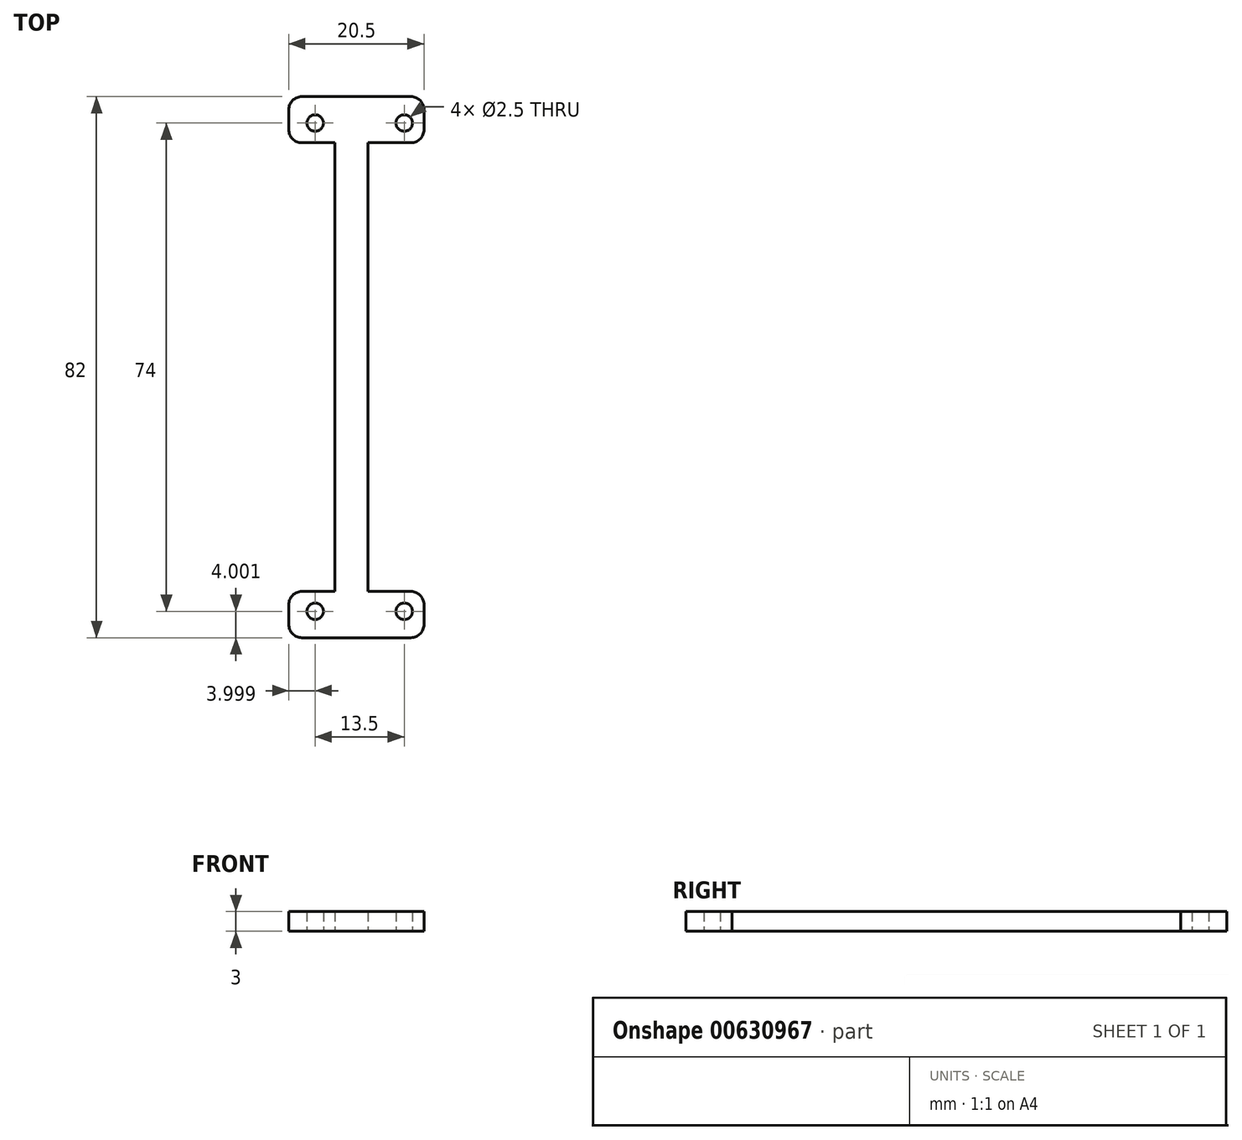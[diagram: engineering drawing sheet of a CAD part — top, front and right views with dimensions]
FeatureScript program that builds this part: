
annotation { "Feature Type Name" : "Feature", "Feature Type Description" : "" }
export const myFeature = defineFeature(function(context is Context, id is Id, definition is map)
    precondition{}
    {
        {
            var Q0;
            Q0=qCreatedBy(makeId("Top.planeOp"),FACE);
            var sketch = newSketch(context, id + "F0", { "sketchPlane" : qUnion([Q0])});
            skCircle(sketch, "E0", {"center": v(-18.35, 41.36) * mm, "radius": 1.25 * mm});
            skCircle(sketch, "E1", {"center": v(-4.85, 41.36) * mm, "radius": 1.25 * mm});
            skCircle(sketch, "E2", {"center": v(-18.35, -32.64) * mm, "radius": 1.25 * mm});
            skCircle(sketch, "E3", {"center": v(-4.85, -32.64) * mm, "radius": 1.25 * mm});
            skLineSegment(sketch, "E4", {"start": v(-20.35, 45.36) * mm, "end": v(-3.85, 45.36) * mm});
            skLineSegment(sketch, "E5", {"start": v(-1.85, 43.36) * mm, "end": v(-1.85, 40.36) * mm});
            skLineSegment(sketch, "E6", {"start": v(-3.85, 38.36) * mm, "end": v(-10.35, 38.36) * mm});
            skLineSegment(sketch, "E7", {"start": v(-10.35, 38.36) * mm, "end": v(-10.35, -29.64) * mm});
            skLineSegment(sketch, "E8", {"start": v(-10.35, -29.64) * mm, "end": v(-3.85, -29.64) * mm});
            skLineSegment(sketch, "E9", {"start": v(-1.85, -31.64) * mm, "end": v(-1.85, -34.64) * mm});
            skLineSegment(sketch, "E10", {"start": v(-3.85, -36.64) * mm, "end": v(-20.35, -36.64) * mm});
            skLineSegment(sketch, "E11", {"start": v(-22.35, -34.64) * mm, "end": v(-22.35, -31.64) * mm});
            skLineSegment(sketch, "E12", {"start": v(-20.35, -29.64) * mm, "end": v(-15.35, -29.64) * mm});
            skLineSegment(sketch, "E13", {"start": v(-15.35, -29.64) * mm, "end": v(-15.35, 38.36) * mm});
            skLineSegment(sketch, "E14", {"start": v(-15.35, 38.36) * mm, "end": v(-20.35, 38.36) * mm});
            skLineSegment(sketch, "E15", {"start": v(-22.35, 40.36) * mm, "end": v(-22.35, 43.36) * mm});
            skPoint(sketch, "E16.visualSharp", {"position": v(-22.35, 45.36) * mm});
            skArc(sketch, "E16.filletArc", {"start": v(-20.35, 45.36) * mm, "mid": v(-21.77, 44.78) * mm, "end": v(-22.35, 43.36) * mm});
            skPoint(sketch, "E17.visualSharp", {"position": v(-1.85, 45.36) * mm});
            skArc(sketch, "E17.filletArc", {"start": v(-1.85, 43.36) * mm, "mid": v(-2.44, 44.78) * mm, "end": v(-3.85, 45.36) * mm});
            skPoint(sketch, "E18.visualSharp", {"position": v(-22.35, -36.64) * mm});
            skArc(sketch, "E18.filletArc", {"start": v(-22.35, -34.64) * mm, "mid": v(-21.77, -36.05) * mm, "end": v(-20.35, -36.64) * mm});
            skPoint(sketch, "E19.visualSharp", {"position": v(-1.85, -36.64) * mm});
            skArc(sketch, "E19.filletArc", {"start": v(-3.85, -36.64) * mm, "mid": v(-2.44, -36.05) * mm, "end": v(-1.85, -34.64) * mm});
            skPoint(sketch, "E20.visualSharp", {"position": v(-22.35, 38.36) * mm});
            skArc(sketch, "E20.filletArc", {"start": v(-22.35, 40.36) * mm, "mid": v(-21.77, 38.95) * mm, "end": v(-20.35, 38.36) * mm});
            skPoint(sketch, "E21.visualSharp", {"position": v(-1.85, 38.36) * mm});
            skArc(sketch, "E21.filletArc", {"start": v(-3.85, 38.36) * mm, "mid": v(-2.44, 38.95) * mm, "end": v(-1.85, 40.36) * mm});
            skPoint(sketch, "E22.visualSharp", {"position": v(-22.35, -29.64) * mm});
            skArc(sketch, "E22.filletArc", {"start": v(-20.35, -29.64) * mm, "mid": v(-21.77, -30.22) * mm, "end": v(-22.35, -31.64) * mm});
            skPoint(sketch, "E23.visualSharp", {"position": v(-1.85, -29.64) * mm});
            skArc(sketch, "E23.filletArc", {"start": v(-1.85, -31.64) * mm, "mid": v(-2.44, -30.22) * mm, "end": v(-3.85, -29.64) * mm});
            skSolve(sketch);
        }
        {
            var Q0;
            Q0=makeQuery(id+"F0.imprint","IMPRINT",FACE,{"disambiguationData":[TD([[makeQuery(id+"F0.imprint","IMPRINT",EDGE,{"derivedFrom":sQuery(id+"F0.wireOp",EDGE,"E0")}),-1.0]])]});
            extrude(context, id + "F1", {"entities" : qUnion([Q0]), "depth" : 3 * mm, "offsetDistance" : 25 * mm});
        }
    });
